# Revit family: Haworth_Masters_Desk_SinglePedBowFront
name_source: partatom
category: Furniture Systems
revit_build: Autodesk Revit 2018 (Build: 20170223_1515(x64)
units: mm (PartAtom-declared; Revit-internal decimal feet)

## family parameters
Always vertical = Yes
Cut with Voids When Loaded = No
OmniClass Number = 23.40.70.14.64.21
OmniClass Title = Systems Furniture
Part Type = Normal
Room Calculation Point = No
Round Connector Dimension = Use Diameter
Shared = No
Work Plane-Based = No

## types (2) — shared parameters
Actual Depth = 36"
Actual Height = 29 1/8"
Actual Width = 72"
Assembly Code = E2020200
Bar Pull = No
Cabinet Finish = Haworth _ Wood _ White Oak
Custom Size = No
Description = Haworth - Masters Desk - Single Ped - Bow Front
Drawer Finish = Haworth _ Wood _ White Oak
Edge Finish = Haworth _ Wood _ White Oak
Linear Pull = No
Manufacturer = Haworth
Max. Width = 78"
Min. Width = 72"
Model = Haworth - Masters Desk - Single Ped - Bow Front
Pull Finish = Haworth _ Metal _ Brushed Aluminum
Revision Number = 3
Size = Verify Final Dim. w/ Haworth
Standard Depth = 36 in.
Standard Widths = 72, 78 in.
Sustainability Info = http://www.haworth.com
URL = www.haworth.com
URL - Product = http://www.haworth.com
Warranty = http://www.haworth.com
Width = 72"
Worksurface Finish = Haworth _ Wood _ White Oak

## per-type parameters (varying)
| type | Classic Pull | Finger Pull |
| Full Overlay Modesty | No | Yes |
| False Pedestal Modesty | Yes | No |

type visibility flags: 2 boolean params named "<type name>" — each type sets only its own to Yes (folded from table)

## geometry (parser evidence)
native form markers: Sweep x14
no freeform markers — native parametric forms only
